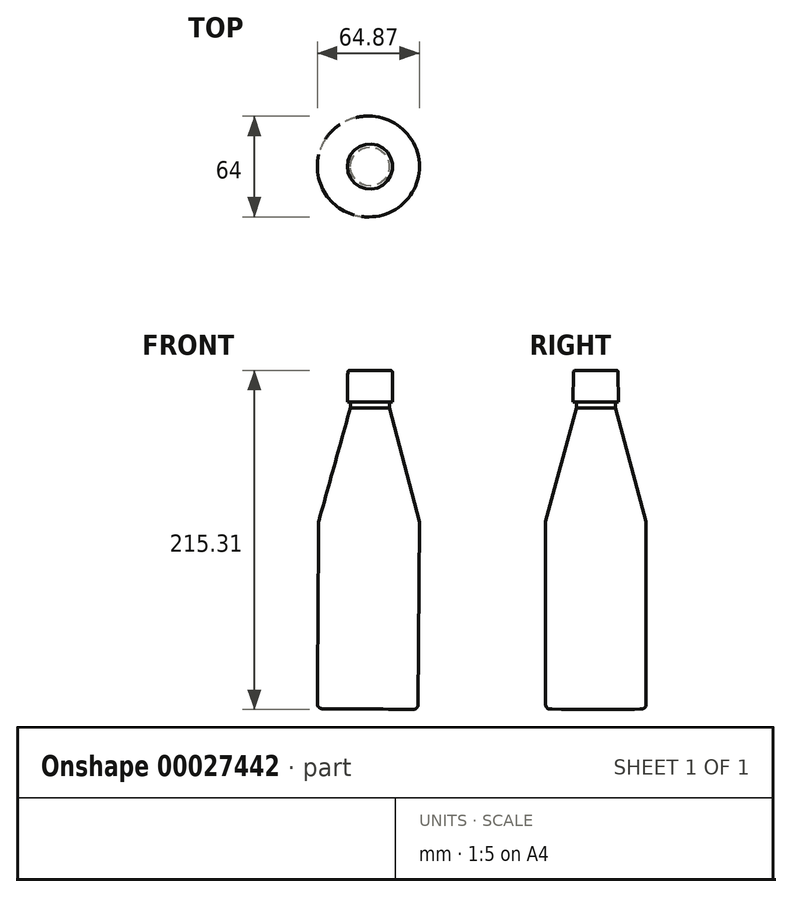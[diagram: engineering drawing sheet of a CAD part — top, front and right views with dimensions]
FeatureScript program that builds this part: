
annotation { "Feature Type Name" : "Feature", "Feature Type Description" : "" }
export const myFeature = defineFeature(function(context is Context, id is Id, definition is map)
    precondition{}
    {
        {
            var Q0;
            Q0=qCreatedBy(makeId("Front.planeOp"),FACE);
            var sketch = newSketch(context, id + "F0", { "sketchPlane" : qUnion([Q0])});
            skLineSegment(sketch, "E0.left", {"start": v(0, 0) * mm, "end": v(1.6, 215) * mm});
            skLineSegment(sketch, "E1", {"start": v(0.89, 118.66) * mm, "end": v(32.89, 118.66) * mm, "construction": true});
            skLineSegment(sketch, "E2", {"start": v(0, 0) * mm, "end": v(32, -0.24) * mm});
            skLineSegment(sketch, "E3", {"start": v(1.6, 215) * mm, "end": v(15.8, 214.89) * mm});
            skLineSegment(sketch, "E4", {"start": v(32.89, 118.66) * mm, "end": v(32, -0.24) * mm});
            skLineSegment(sketch, "E5", {"start": v(15.8, 214.89) * mm, "end": v(15.8, 194.89) * mm});
            skLineSegment(sketch, "E6", {"start": v(15.8, 194.89) * mm, "end": v(13.8, 194.89) * mm});
            skLineSegment(sketch, "E7", {"start": v(13.8, 194.89) * mm, "end": v(13.8, 191.19) * mm});
            skLineSegment(sketch, "E8", {"start": v(13.8, 191.19) * mm, "end": v(32.89, 118.66) * mm});
            skSolve(sketch);
        }
        {
            var Q0;
            Q0 = qSketchRegion(id + "F0", true);
            var Q1;
            Q1=sQuery(id+"F0.wireOp",EDGE,"E0.left");
            revolve(context, id + "F1", {"entities" : qUnion([Q0]), "axis" : qUnion([Q1]), "revolveType" : RevolveType.FULL});
        }
        {
            var Q0;
            Q0=makeQuery(id+"F1.opRevolve","SWEPT_EDGE",EDGE,{"disambiguationData":[OSD([sQuery(id+"F0.wireOp",EDGE,"E2"),sQuery(id+"F0.wireOp",EDGE,"E4")])]});
            fillet(context, id + "F2", {"entities" : qUnion([Q0]), "radius" : 3 * mm, "tangentPropagation" : true, "allowEdgeOverflow" : false});
        }
        {
            var Q0;
            Q0=makeQuery(id+"F1.opRevolve","SWEPT_EDGE",EDGE,{"disambiguationData":[OSD([sQuery(id+"F0.wireOp",EDGE,"E4"),sQuery(id+"F0.wireOp",EDGE,"E8")])]});
            fillet(context, id + "F3", {"entities" : qUnion([Q0]), "radius" : 2 * mm, "tangentPropagation" : true, "allowEdgeOverflow" : false});
        }
        {
            var Q0;
            Q0=makeQuery(id+"F1.opRevolve","SWEPT_EDGE",EDGE,{"disambiguationData":[OSD([sQuery(id+"F0.wireOp",EDGE,"E3"),sQuery(id+"F0.wireOp",EDGE,"E5")])]});
            fillet(context, id + "F4", {"entities" : qUnion([Q0]), "radius" : 1 * mm, "tangentPropagation" : true, "allowEdgeOverflow" : false});
        }
    });
